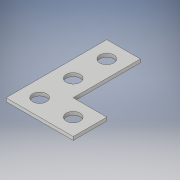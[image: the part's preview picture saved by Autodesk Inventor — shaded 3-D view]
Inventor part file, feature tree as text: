
AUTODESK INVENTOR PART (.ipt)
format: ipt  version: 2018 (Build 220112000, 112)  size: 119,296 bytes
history: native  units: in
note: dims shown in document units (in); Inventor stores cm internally (conversion verified against a paired STEP export)
features: extrude x1, sketch x1
ambient origin geometry x8: Origin, YZ Plane, XZ Plane, XY Plane, X Axis, Y Axis, Z Axis, Center Point
bodies: Solid1 (feature_tree)
feature tree (2):
  extrude  "Extrusion1"  Depth=1.0in
  sketch  "Sketch1"  dims[d0=3.0in d1=1.0in d2=1.0in d3=1.0in d5=1.5in d7=1.0in d8=1.0in d11=0.5in d12=0.5in d13=0.5in d14=0.4167in d15=0.4167in d16=0.4167in d17=0.4167in d18=0.5in d19=1.0in d20=0.5in d21=0.1in d22=0.0in]
